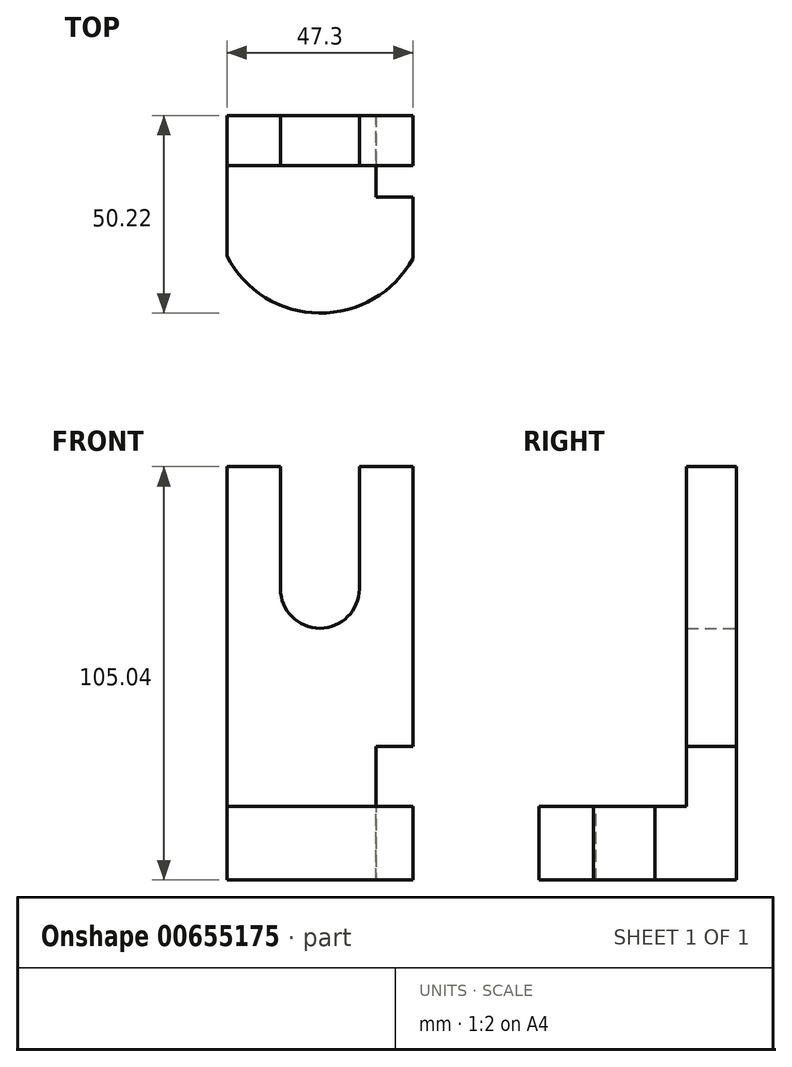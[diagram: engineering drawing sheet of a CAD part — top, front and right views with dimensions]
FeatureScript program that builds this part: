
annotation { "Feature Type Name" : "Feature", "Feature Type Description" : "" }
export const myFeature = defineFeature(function(context is Context, id is Id, definition is map)
    precondition{}
    {
        {
            var Q0;
            Q0=qCreatedBy(makeId("Front.planeOp"),FACE);
            var sketch = newSketch(context, id + "F0", { "sketchPlane" : qUnion([Q0])});
            skLineSegment(sketch, "E0.bottom", {"start": v(-23.65, 52.52) * mm, "end": v(-10.01, 52.52) * mm});
            skLineSegment(sketch, "E0.top", {"start": v(-23.65, -52.52) * mm, "end": v(23.65, -52.52) * mm});
            skLineSegment(sketch, "E0.left", {"start": v(-23.65, 52.52) * mm, "end": v(-23.65, -52.52) * mm});
            skLineSegment(sketch, "E0.right", {"start": v(23.65, 52.52) * mm, "end": v(23.65, -52.52) * mm});
            skPoint(sketch, "E0.middle", {"position": v(0, 0) * mm});
            skLineSegment(sketch, "E1.left", {"start": v(-10.01, 52.52) * mm, "end": v(-10.01, 21.47) * mm});
            skLineSegment(sketch, "E1.right", {"start": v(10.01, 52.52) * mm, "end": v(10.01, 21.47) * mm});
            skArc(sketch, "E2", {"start": v(-10.01, 21.47) * mm, "mid": v(0, 11.46) * mm, "end": v(10.01, 21.47) * mm});
            skLineSegment(sketch, "E3.trimOffspring", {"start": v(10.01, 52.52) * mm, "end": v(23.65, 52.52) * mm});
            skSolve(sketch);
        }
        {
            var Q0;
            Q0 = qSketchRegion(id + "F0", true);
            extrude(context, id + "F1", {"entities" : qUnion([Q0]), "depth" : 12.7 * mm, "offsetDistance" : 25.4 * mm});
        }
        {
            var Q0;
            Q0=makeQuery(id+"F1.opExtrude","CAP_FACE",FACE,{"disambiguationData":[OSD([sQuery(id+"F0.wireOp",EDGE,"E0.bottom"),sQuery(id+"F0.wireOp",EDGE,"E0.top"),sQuery(id+"F0.wireOp",EDGE,"E0.left"),sQuery(id+"F0.wireOp",EDGE,"E0.right"),sQuery(id+"F0.wireOp",EDGE,"E1.left"),sQuery(id+"F0.wireOp",EDGE,"E1.right"),sQuery(id+"F0.wireOp",EDGE,"E2"),sQuery(id+"F0.wireOp",EDGE,"E3.trimOffspring")])],"isStart":false});
            var sketch = newSketch(context, id + "F2", { "sketchPlane" : qUnion([Q0])});
            skLineSegment(sketch, "E4.bottom", {"start": v(-23.65, -52.52) * mm, "end": v(23.65, -52.52) * mm});
            skLineSegment(sketch, "E4.top", {"start": v(-23.65, -33.82) * mm, "end": v(23.65, -33.82) * mm});
            skLineSegment(sketch, "E4.left", {"start": v(-23.65, -52.52) * mm, "end": v(-23.65, -33.82) * mm});
            skLineSegment(sketch, "E4.right", {"start": v(23.65, -52.52) * mm, "end": v(23.65, -33.82) * mm});
            skSolve(sketch);
        }
        {
            var Q0;
            Q0 = qSketchRegion(id + "F2", true);
            extrude(context, id + "F3", {"entities" : qUnion([Q0]), "operationType" : NewBodyOperationType.ADD, "depth" : 38.35 * mm, "offsetDistance" : 25.4 * mm});
        }
        {
            var Q0;
            Q0=makeQuery(id+"F3.opExtrude","SWEPT_FACE",FACE,{"disambiguationData":[OSD([sQuery(id+"F2.wireOp",EDGE,"E4.top")])]});
            var sketch = newSketch(context, id + "F4", { "sketchPlane" : qUnion([Q0])});
            skArc(sketch, "E5", {"start": v(-23.65, -35.77) * mm, "mid": v(-0.18, -50.21) * mm, "end": v(23.65, -36.37) * mm});
            skSolve(sketch);
        }
        {
            var Q0;
            {var subQ0=sQuery(id+"F4.wireOp",EDGE,"E5");Q0=makeQuery(id+"F4.imprint","IMPRINT",FACE,{"disambiguationData":[TD([[makeQuery(id+"F4.imprint","IMPRINT",EDGE,{"derivedFrom":subQ0}),-1.0]])]});}
            extrude(context, id + "F5", {"entities" : qUnion([Q0]), "operationType" : NewBodyOperationType.REMOVE, "oppositeDirection" : true, "depth" : 25.4 * mm, "offsetDistance" : 25.4 * mm});
        }
        {
            var Q0;
            Q0=makeQuery(id+"F3.boolean.opBoolean","MERGE",FACE,{"derivedFrom":[makeQuery(id+"F1.opExtrude","SWEPT_FACE",FACE,{"disambiguationData":[OSD([sQuery(id+"F0.wireOp",EDGE,"E0.right")])]}),makeQuery(id+"F3.opExtrude","SWEPT_FACE",FACE,{"disambiguationData":[OSD([sQuery(id+"F2.wireOp",EDGE,"E4.right")])]})]});
            var sketch = newSketch(context, id + "F6", { "sketchPlane" : qUnion([Q0])});
            skLineSegment(sketch, "E6.bottom", {"start": v(0, -52.52) * mm, "end": v(-20.73, -52.52) * mm});
            skLineSegment(sketch, "E6.top", {"start": v(0, -18.56) * mm, "end": v(-20.73, -18.56) * mm});
            skLineSegment(sketch, "E6.left", {"start": v(0, -52.52) * mm, "end": v(0, -18.56) * mm});
            skLineSegment(sketch, "E6.right", {"start": v(-20.73, -52.52) * mm, "end": v(-20.73, -18.56) * mm});
            skSolve(sketch);
        }
        {
            var Q0;
            Q0 = qSketchRegion(id + "F6", true);
            extrude(context, id + "F7", {"entities" : qUnion([Q0]), "operationType" : NewBodyOperationType.REMOVE, "oppositeDirection" : true, "depth" : 9.4 * mm, "offsetDistance" : 25.4 * mm});
        }
    });
